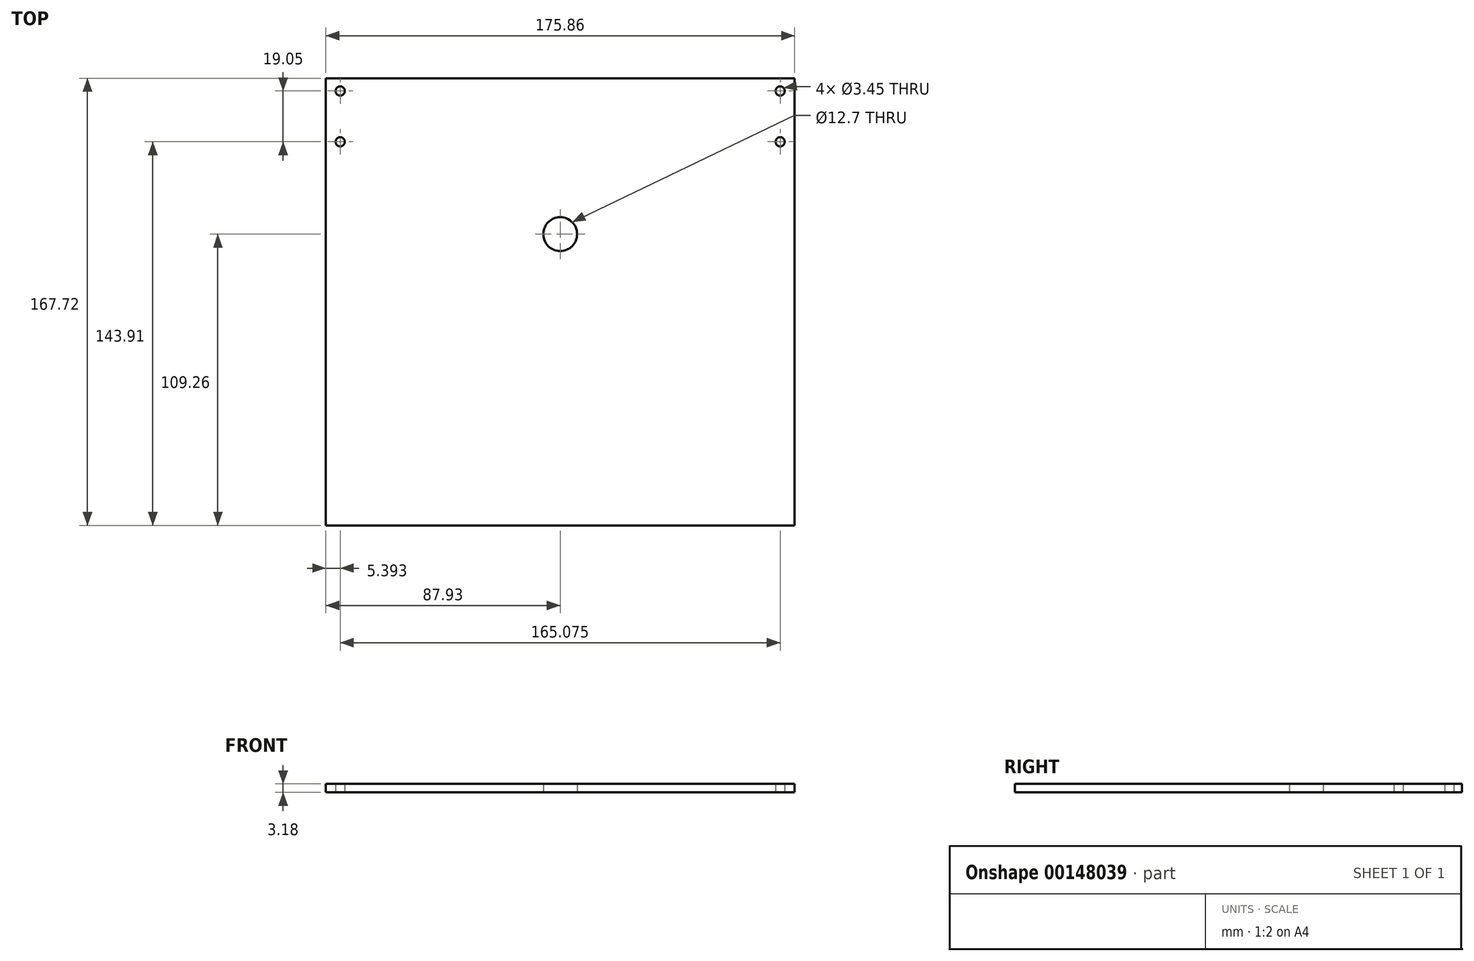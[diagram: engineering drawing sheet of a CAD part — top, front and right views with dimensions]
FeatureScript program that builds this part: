
annotation { "Feature Type Name" : "Feature", "Feature Type Description" : "" }
export const myFeature = defineFeature(function(context is Context, id is Id, definition is map)
    precondition{}
    {
        {
            var Q0;
            Q0=qCreatedBy(makeId("Top.planeOp"),FACE);
            var sketch = newSketch(context, id + "F0", { "sketchPlane" : qUnion([Q0])});
            skPoint(sketch, "E0.middle", {"position": v(0, 0) * mm});
            skLineSegment(sketch, "E1", {"start": v(0, 0) * mm, "end": v(0, 0) * mm});
            skLineSegment(sketch, "E2.bottom", {"start": v(-87.93, 83.86) * mm, "end": v(87.93, 83.86) * mm});
            skLineSegment(sketch, "E2.top", {"start": v(-87.93, -83.86) * mm, "end": v(87.93, -83.86) * mm});
            skLineSegment(sketch, "E2.left", {"start": v(-87.93, 83.86) * mm, "end": v(-87.93, -83.86) * mm});
            skLineSegment(sketch, "E2.right", {"start": v(87.93, 83.86) * mm, "end": v(87.93, -83.86) * mm});
            skLineSegment(sketch, "E3", {"start": v(-87.93, 79.1) * mm, "end": v(-82.54, 79.1) * mm, "construction": true});
            skLineSegment(sketch, "E4", {"start": v(-82.54, 79.1) * mm, "end": v(-82.54, 83.86) * mm, "construction": true});
            skLineSegment(sketch, "E5", {"start": v(82.54, 83.86) * mm, "end": v(82.54, 79.1) * mm, "construction": true});
            skLineSegment(sketch, "E6", {"start": v(82.54, 79.1) * mm, "end": v(87.93, 79.1) * mm, "construction": true});
            skLineSegment(sketch, "E7", {"start": v(82.54, 79.1) * mm, "end": v(82.54, 60.05) * mm, "construction": true});
            skLineSegment(sketch, "E8", {"start": v(-82.54, 79.1) * mm, "end": v(-82.54, 60.05) * mm, "construction": true});
            skCircle(sketch, "E9", {"center": v(-82.54, 79.1) * mm, "radius": 1.73 * mm});
            skCircle(sketch, "E10", {"center": v(-82.54, 60.05) * mm, "radius": 1.73 * mm});
            skCircle(sketch, "E11", {"center": v(82.54, 60.05) * mm, "radius": 1.73 * mm});
            skCircle(sketch, "E12", {"center": v(82.54, 79.1) * mm, "radius": 1.73 * mm});
            skLineSegment(sketch, "E13", {"start": v(0, 0) * mm, "end": v(0, 25.4) * mm, "construction": true});
            skCircle(sketch, "E14", {"center": v(0, 25.4) * mm, "radius": 6.35 * mm});
            skSolve(sketch);
        }
        {
            var Q0;
            Q0=qSketchRegion(id+"F0",true);
            extrude(context, id + "F1", {"entities" : qUnion([Q0]), "depth" : 3.17 * mm});
        }
    });
